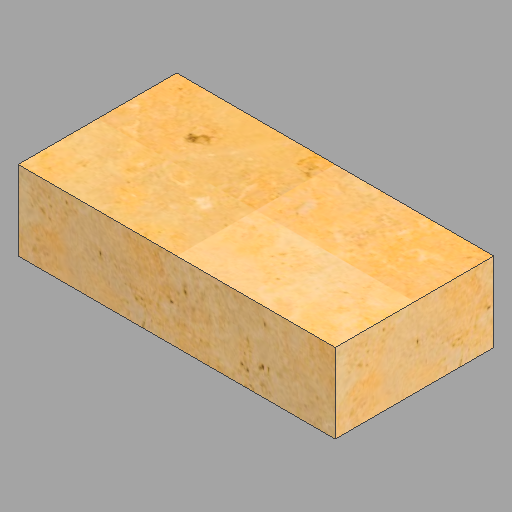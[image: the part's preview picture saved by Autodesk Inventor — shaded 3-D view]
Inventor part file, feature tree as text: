
AUTODESK INVENTOR PART (.ipt)
format: ipt  version: 2023 (Build 270158030, 158C)  size: 310,272 bytes
history: native  units: in
note: dims shown in document units (in); Inventor stores cm internally (conversion verified against a paired STEP export)
features: other x1, extrude x1, sketch x1
ambient origin geometry x8: Origin, YZ Plane, XZ Plane, XY Plane, X Axis, Y Axis, Z Axis, Center Point
bodies: Solid1 (feature_tree)
feature tree (3):
  other  "4x8x2 - 39"
  extrude  "Extrusion1"  Depth=4.0in
  sketch  "Sketch1"  dims[d0=8.0in d1=4.0in d2=2.0in d3=0.0in]
